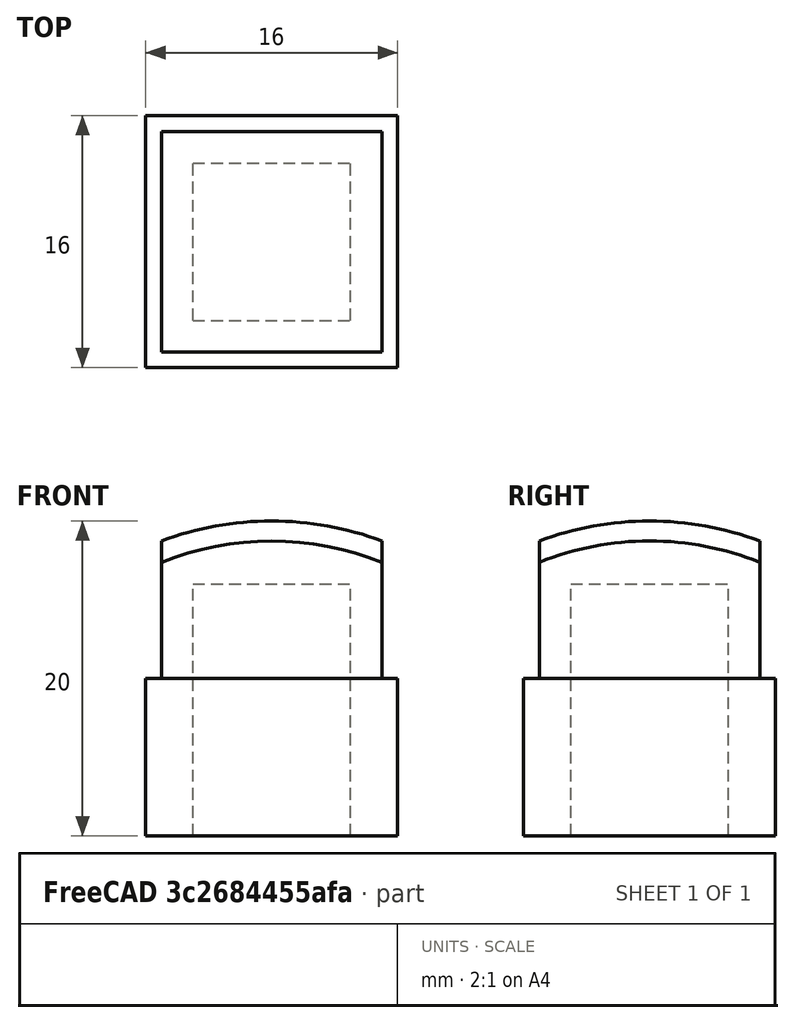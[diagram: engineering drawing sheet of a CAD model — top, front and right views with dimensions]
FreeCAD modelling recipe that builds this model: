
FCSTD DOCUMENT  (FreeCAD 0.18.3R)
Label: curved_surface
License: All rights reserved
LicenseURL: http://en.wikipedia.org/wiki/All_rights_reserved
objects: Part::Box×3, Part::Sphere×1, Part::MultiCommon×1, Part::Fuse×1, Part::Cut×1
note: 7 computed .brp shape members not serialized (recipe doc carries the construction recipe); baked Part::Feature solids carry a one-line shape summary decoded from their .brp

FEATURE [Part::Box] Box  label="Cube"
  AttacherType = Attacher::AttachEngine3D
  Height = 10
  Length = 16
  Placement = pos=(-8,-8,0) rot=(0,0,1;0rad)
  Width = 16
FEATURE [Part::Box] Box001  label="Cubo"
  AttacherType = Attacher::AttachEngine3D
  Height = 10
  Length = 14
  Placement = pos=(-7,-7,10) rot=(0,0,1;0rad)
  Width = 14
FEATURE [Part::Sphere] Sphere  label="Esfera"
  Angle1 = -90
  Angle2 = 90
  Angle3 = 360
  AttacherType = Attacher::AttachEngine3D
  Radius = 20
FEATURE [Part::MultiCommon] Common
  Shapes = -> [Sphere,Box001]
FEATURE [Part::Fuse] Fusion
  Base = -> Box
  Tool = -> Common
FEATURE [Part::Box] Box002  label="Cube001"
  AttacherType = Attacher::AttachEngine3D
  Height = 16
  Length = 10
  Placement = pos=(-5,-5,0) rot=(0,0,1;0rad)
  Width = 10
FEATURE [Part::Cut] Cut
  Base = -> Fusion
  Tool = -> Box002
